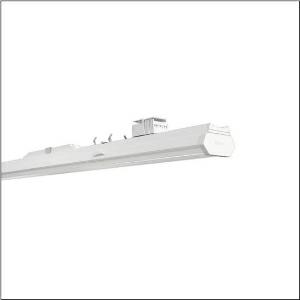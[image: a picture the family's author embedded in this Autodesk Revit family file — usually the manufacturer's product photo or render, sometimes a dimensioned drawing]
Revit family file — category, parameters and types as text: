
# Revit family: licross_r__11_protected_ho_51tp13cn4dxr_fe54
name_source: partatom
category: Lighting Fixtures
units: mm (PartAtom-declared; Revit-internal decimal feet)

## family parameters
Cut with Voids When Loaded = No
Host = Face
Light Source = No
Part Type = Normal
Room Calculation Point = No
Round Connector Dimension = Use Diameter
Shared = No

## types (1)
- --- (1 x LED, 13280 lm, 76.4 W, 4000K)
    Apparent Load = 76 VA
    CIE Flux Codes = 89 96 99 100 99
    Color Rendering = 80
    Color Temperature = 4000K
    Default Elevation = 1800 mm
    Description = Licross® 11 Protected HOluminaire insert, length: 1.500mm, width: 90mm, height: 101mm, LED rated luminous flux: 13.280lm, light colour: 840, control gear: ON/OFF Multilumen, CLOi, control gear: ECG Multilumen, with plug, 3-pole, with phase selection, mains connection: 220..240V, AC, 50/60Hz, halogen-free wiring, primary optical cover: cover, of PMMA, light emission: direct distribution, protection rating (complete): IP64, insulation class (complete): insulation class I (protective earthing), certification: CE, ENEC, VDE, protection symbol: D if used in an environment with conductive dust loads with corresponding accessories, permissible ambient temperature for indoor applications: -35..+40°C, reducing of maximum allowable ambient temperature of 5°C with ceiling mounting, corresponds to IFS (International Featured Standards) requirements for safety and quality in the food industry, packaging unit: 1 piece
    Height = 92 mm
    Lamp = 1 x LED
    Lamp Light Flux = 13280 lm
    Lamp Power = 76.4 W
    Lamp count = 1
    Length = 1500 mm
    Luminous efficacy = 174 lm/W
    Manufacturer = Siteco
    ModVariant = No
    Model = 51TP13CN4DXR
    Mounting Place = Ceiling
    Mounting Type = Pendant
    Number of Poles = 1
    OnlyDefault = Yes
    Power Factor = 1
    Product Name = Licross® 11 Protected HO
    Product group = luminaire insert
    ProductGroupID = 902
    Protection Class = Protection class I
    Protection Degree = IP 64
    RLX_Detail_Level = 1
    RlxData = <blob elided: 21769 chars, md5=1666e5d1>
    Socket = socket
    Standby Power = 0 W
    System Light Flux = 13280 lm
    System Power = 76 W
    Type Comments = factory setting: luminous flux: 100 % | (A | C | E) | 177 mA
    Type Image = l_1256148.jpg
    URL = http://relux.com
    VarID = @adj_137605
    Voltage = 0 V
    Weight = 0.00 kg
    Width = 88 mm

## geometry (parser evidence)
native form markers: Blend x4, Sweep x12
no freeform markers — native parametric forms only
